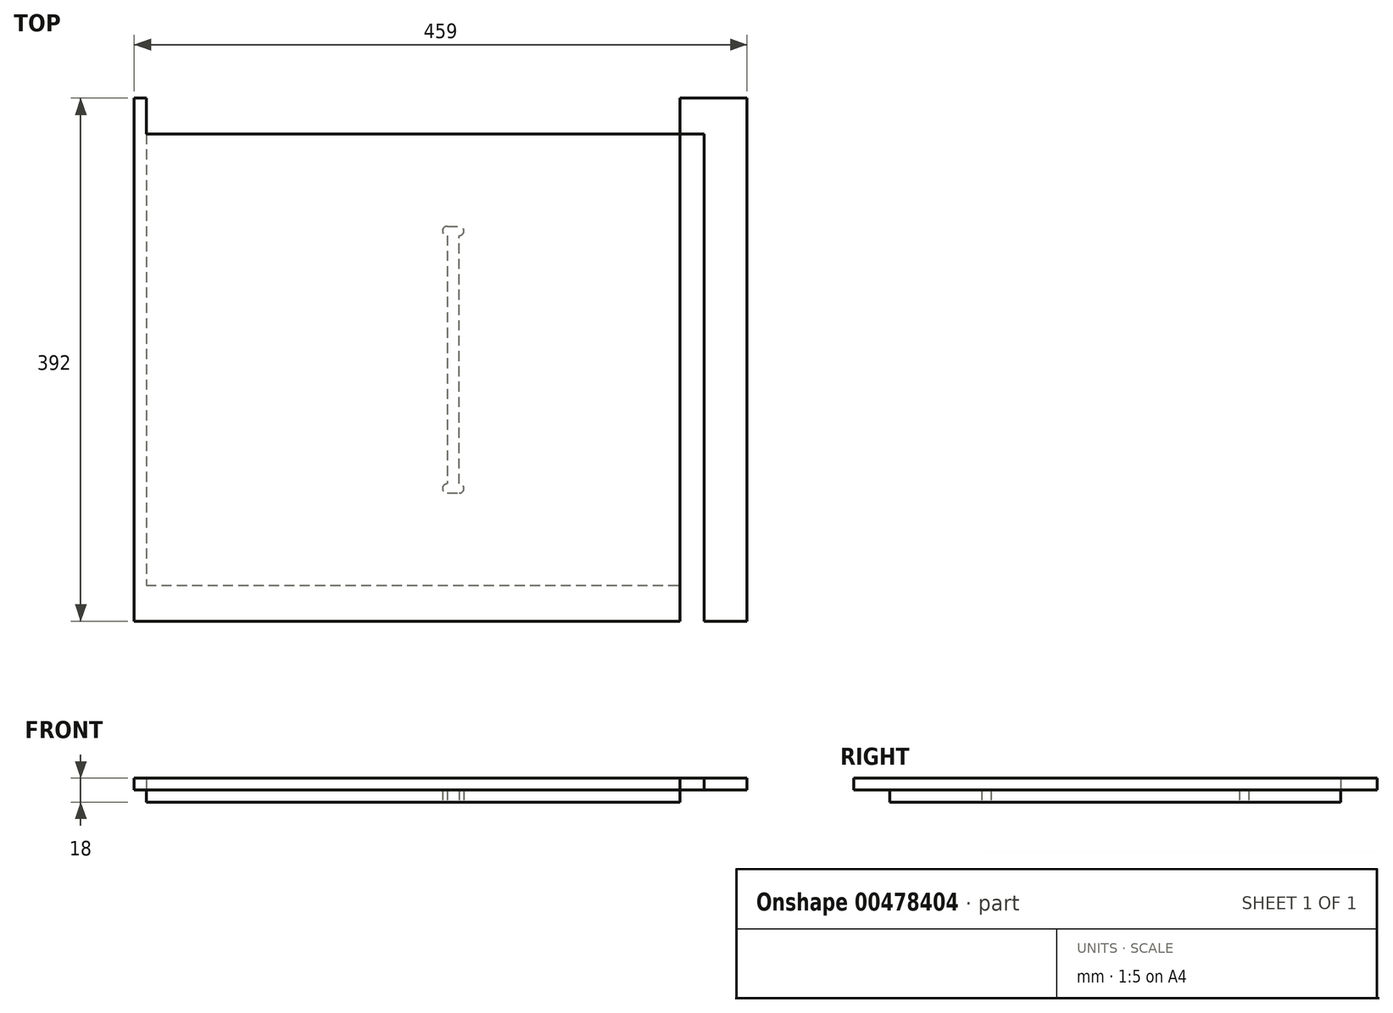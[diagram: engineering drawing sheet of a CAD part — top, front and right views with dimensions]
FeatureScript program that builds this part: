
annotation { "Feature Type Name" : "Feature", "Feature Type Description" : "" }
export const myFeature = defineFeature(function(context is Context, id is Id, definition is map)
    precondition{}
    {
        {
            var Q0;
            Q0=qCreatedBy(makeId("Top.planeOp"),FACE);
            var sketch = newSketch(context, id + "F0", { "sketchPlane" : qUnion([Q0])});
            skLineSegment(sketch, "E0.bottom", {"start": v(-966.15, 22.1) * mm, "end": v(-736.65, 22.1) * mm});
            skPoint(sketch, "E1", {"position": v(-736.65, 22.1) * mm});
            skPoint(sketch, "E2", {"position": v(-966.15, 22.1) * mm});
            skLineSegment(sketch, "E3.0", {"start": v(-966.15, -4.9) * mm, "end": v(133.85, -4.9) * mm});
            skLineSegment(sketch, "E4.0", {"start": v(-966.15, -369.9) * mm, "end": v(-736.65, -369.9) * mm});
            skLineSegment(sketch, "E5", {"start": v(-736.65, 22.1) * mm, "end": v(-736.65, -369.9) * mm, "construction": true});
            skLineSegment(sketch, "E6", {"start": v(-966.15, 22.1) * mm, "end": v(-966.15, -369.9) * mm});
            skLineSegment(sketch, "E7.0", {"start": v(-957.15, 22.1) * mm, "end": v(-957.15, -369.9) * mm});
            skLineSegment(sketch, "E8.0", {"start": v(-966.15, -342.9) * mm, "end": v(133.85, -342.9) * mm});
            skLineSegment(sketch, "E9.MirrorCS", {"start": v(-507.15, 22.1) * mm, "end": v(-507.15, -369.9) * mm});
            skPoint(sketch, "E10.MirrorP", {"position": v(-507.15, 22.1) * mm});
            skLineSegment(sketch, "E11.MirrorCS", {"start": v(-507.15, 22.1) * mm, "end": v(-736.65, 22.1) * mm});
            skLineSegment(sketch, "E12.MirrorCS", {"start": v(-507.15, -4.9) * mm, "end": v(-1607.15, -4.9) * mm});
            skLineSegment(sketch, "E13.MirrorCS", {"start": v(-507.15, -342.9) * mm, "end": v(-1607.15, -342.9) * mm});
            skLineSegment(sketch, "E14.MirrorCS", {"start": v(-507.15, -369.9) * mm, "end": v(-736.65, -369.9) * mm});
            skLineSegment(sketch, "E15", {"start": v(-731.6, -73.9) * mm, "end": v(-722.6, -73.9) * mm});
            skArc(sketch, "E16", {"start": v(-731.6, -73.9) * mm, "mid": v(-735.1, -77.4) * mm, "end": v(-731.6, -80.9) * mm});
            skArc(sketch, "E17", {"start": v(-722.6, -80.9) * mm, "mid": v(-719.1, -77.4) * mm, "end": v(-722.6, -73.9) * mm});
            skLineSegment(sketch, "E18.trimOffspring", {"start": v(-722.6, -80.9) * mm, "end": v(-722.6, -173.9) * mm});
            skLineSegment(sketch, "E19", {"start": v(-731.6, -80.9) * mm, "end": v(-731.6, -173.9) * mm});
            skLineSegment(sketch, "E20.MirrorCS", {"start": v(-722.6, -266.9) * mm, "end": v(-722.6, -173.9) * mm});
            skLineSegment(sketch, "E21.MirrorCS", {"start": v(-731.6, -266.9) * mm, "end": v(-731.6, -173.9) * mm});
            skArc(sketch, "E22.MirrorCS", {"start": v(-731.6, -273.9) * mm, "mid": v(-735.1, -270.4) * mm, "end": v(-731.6, -266.9) * mm});
            skLineSegment(sketch, "E23.MirrorCS", {"start": v(-731.6, -273.9) * mm, "end": v(-722.6, -273.9) * mm});
            skArc(sketch, "E24.MirrorCS", {"start": v(-722.6, -266.9) * mm, "mid": v(-719.1, -270.4) * mm, "end": v(-722.6, -273.9) * mm});
            skLineSegment(sketch, "E25.0", {"start": v(-539.15, 22.1) * mm, "end": v(-539.15, -369.9) * mm});
            skLineSegment(sketch, "E26.0", {"start": v(-557.15, 22.1) * mm, "end": v(-557.15, -369.9) * mm});
            skSolve(sketch);
        }
        {
            var Q0;
            {var subQ0=sQuery(id+"F0.wireOp",EDGE,"E6");var subQ1=sQuery(id+"F0.wireOp",EDGE,"E0.bottom");var subQ2=makeQuery(id+"F0.imprint","INTERSECT",VERTEX,{"derivedFrom":[subQ1,subQ0]});Q0=makeQuery(id+"F0.imprint","IMPRINT",FACE,{"disambiguationData":[TD([[makeQuery(id+"F0.imprint","IMPRINT",EDGE,{"disambiguationData":[TD([[subQ2,-1.0]])],"derivedFrom":subQ1}),-1.0]])]});}
            var Q1;
            {var subQ0=sQuery(id+"F0.wireOp",EDGE,"E6");var subQ1=sQuery(id+"F0.wireOp",EDGE,"E4.0");var subQ2=makeQuery(id+"F0.imprint","INTERSECT",VERTEX,{"derivedFrom":[subQ1,subQ0]});Q1=makeQuery(id+"F0.imprint","IMPRINT",FACE,{"disambiguationData":[TD([[makeQuery(id+"F0.imprint","IMPRINT",EDGE,{"disambiguationData":[TD([[subQ2,-1.0]])],"derivedFrom":subQ1}),1.0]])]});}
            var Q2;
            {var subQ0=sQuery(id+"F0.wireOp",EDGE,"E14.MirrorCS");var subQ1=sQuery(id+"F0.wireOp",EDGE,"E4.0");var subQ2=makeQuery(id+"F0.imprint","INTERSECT",VERTEX,{"derivedFrom":[subQ1,subQ0]});Q2=makeQuery(id+"F0.imprint","IMPRINT",FACE,{"disambiguationData":[TD([[makeQuery(id+"F0.imprint","IMPRINT",EDGE,{"disambiguationData":[TD([[subQ2,1.0]])],"derivedFrom":subQ1}),1.0]])]});}
            var Q3;
            {var subQ0=sQuery(id+"F0.wireOp",EDGE,"E25.0");var subQ1=sQuery(id+"F0.wireOp",EDGE,"E12.MirrorCS");var subQ2=makeQuery(id+"F0.imprint","INTERSECT",VERTEX,{"derivedFrom":[subQ1,subQ0]});Q3=makeQuery(id+"F0.imprint","IMPRINT",FACE,{"disambiguationData":[TD([[makeQuery(id+"F0.imprint","IMPRINT",EDGE,{"disambiguationData":[TD([[subQ2,-1.0]])],"derivedFrom":subQ1}),1.0]])]});}
            var Q4;
            {var subQ5=sQuery(id+"F0.wireOp",EDGE,"E0.bottom");var subQ7=sQuery(id+"F0.wireOp",EDGE,"E11.MirrorCS");var subQ9=makeQuery(id+"F0.imprint","INTERSECT",VERTEX,{"derivedFrom":[subQ5,subQ7]});Q4=makeQuery(id+"F0.imprint","IMPRINT",FACE,{"disambiguationData":[TD([[makeQuery(id+"F0.imprint","IMPRINT",EDGE,{"disambiguationData":[TD([[subQ9,1.0]])],"derivedFrom":subQ5}),-1.0]])]});}
            var Q5;
            Q5=makeQuery(id+"F0.imprint","IMPRINT",FACE,{"disambiguationData":[TD([[makeQuery(id+"F0.imprint","IMPRINT",EDGE,{"derivedFrom":sQuery(id+"F0.wireOp",EDGE,"E15")}),1.0]])]});
            var Q6;
            {var subQ0=sQuery(id+"F0.wireOp",EDGE,"E12.MirrorCS");var subQ1=sQuery(id+"F0.wireOp",EDGE,"E9.MirrorCS");var subQ2=makeQuery(id+"F0.imprint","INTERSECT",VERTEX,{"derivedFrom":[subQ1,subQ0]});Q6=makeQuery(id+"F0.imprint","IMPRINT",FACE,{"disambiguationData":[TD([[makeQuery(id+"F0.imprint","IMPRINT",EDGE,{"disambiguationData":[TD([[subQ2,1.0]])],"derivedFrom":subQ1}),-1.0]])]});}
            var Q7;
            {var subQ0=sQuery(id+"F0.wireOp",EDGE,"E12.MirrorCS");var subQ1=sQuery(id+"F0.wireOp",EDGE,"E9.MirrorCS");var subQ2=makeQuery(id+"F0.imprint","INTERSECT",VERTEX,{"derivedFrom":[subQ1,subQ0]});Q7=makeQuery(id+"F0.imprint","IMPRINT",FACE,{"disambiguationData":[TD([[makeQuery(id+"F0.imprint","IMPRINT",EDGE,{"disambiguationData":[TD([[subQ2,-1.0]])],"derivedFrom":subQ1}),-1.0]])]});}
            var Q8;
            {var subQ0=sQuery(id+"F0.wireOp",EDGE,"E12.MirrorCS");var subQ1=sQuery(id+"F0.wireOp",EDGE,"E6");var subQ2=makeQuery(id+"F0.imprint","INTERSECT",VERTEX,{"derivedFrom":[subQ1,subQ0]});Q8=makeQuery(id+"F0.imprint","IMPRINT",FACE,{"disambiguationData":[TD([[makeQuery(id+"F0.imprint","IMPRINT",EDGE,{"disambiguationData":[TD([[subQ2,-1.0]])],"derivedFrom":subQ1}),1.0]])]});}
            var Q9;
            Q9=makeQuery(id+"F0.imprint","IMPRINT",FACE,{"disambiguationData":[TD([[makeQuery(id+"F0.imprint","IMPRINT",EDGE,{"derivedFrom":sQuery(id+"F0.wireOp",EDGE,"E15")}),-1.0]])]});
            var Q10;
            {var subQ0=sQuery(id+"F0.wireOp",EDGE,"E25.0");var subQ1=sQuery(id+"F0.wireOp",EDGE,"E13.MirrorCS");var subQ2=makeQuery(id+"F0.imprint","INTERSECT",VERTEX,{"derivedFrom":[subQ1,subQ0]});Q10=makeQuery(id+"F0.imprint","IMPRINT",FACE,{"disambiguationData":[TD([[makeQuery(id+"F0.imprint","IMPRINT",EDGE,{"disambiguationData":[TD([[subQ2,-1.0]])],"derivedFrom":subQ1}),1.0]])]});}
            var Q11;
            {var subQ0=sQuery(id+"F0.wireOp",EDGE,"E25.0");var subQ1=sQuery(id+"F0.wireOp",EDGE,"E11.MirrorCS");var subQ2=makeQuery(id+"F0.imprint","INTERSECT",VERTEX,{"derivedFrom":[subQ1,subQ0]});Q11=makeQuery(id+"F0.imprint","IMPRINT",FACE,{"disambiguationData":[TD([[makeQuery(id+"F0.imprint","IMPRINT",EDGE,{"disambiguationData":[TD([[subQ2,-1.0]])],"derivedFrom":subQ1}),1.0]])]});}
            var Q12;
            {var subQ0=sQuery(id+"F0.wireOp",EDGE,"E13.MirrorCS");var subQ1=sQuery(id+"F0.wireOp",EDGE,"E9.MirrorCS");var subQ2=makeQuery(id+"F0.imprint","INTERSECT",VERTEX,{"derivedFrom":[subQ1,subQ0]});Q12=makeQuery(id+"F0.imprint","IMPRINT",FACE,{"disambiguationData":[TD([[makeQuery(id+"F0.imprint","IMPRINT",EDGE,{"disambiguationData":[TD([[subQ2,-1.0]])],"derivedFrom":subQ1}),-1.0]])]});}
            extrude(context, id + "F1", {"entities" : qUnion([Q0, Q1, Q2, Q3, Q4, Q5, Q6, Q7, Q8, Q9, Q10, Q11, Q12]), "depth" : 18 * mm});
        }
        {
            var Q0;
            {var subQ0=sQuery(id+"F0.wireOp",EDGE,"E6");var subQ1=sQuery(id+"F0.wireOp",EDGE,"E4.0");var subQ2=makeQuery(id+"F0.imprint","INTERSECT",VERTEX,{"derivedFrom":[subQ1,subQ0]});Q0=makeQuery(id+"F0.imprint","IMPRINT",FACE,{"disambiguationData":[TD([[makeQuery(id+"F0.imprint","IMPRINT",EDGE,{"disambiguationData":[TD([[subQ2,-1.0]])],"derivedFrom":subQ1}),1.0]])]});}
            var Q1;
            {var subQ0=sQuery(id+"F0.wireOp",EDGE,"E12.MirrorCS");var subQ1=sQuery(id+"F0.wireOp",EDGE,"E6");var subQ2=makeQuery(id+"F0.imprint","INTERSECT",VERTEX,{"derivedFrom":[subQ1,subQ0]});Q1=makeQuery(id+"F0.imprint","IMPRINT",FACE,{"disambiguationData":[TD([[makeQuery(id+"F0.imprint","IMPRINT",EDGE,{"disambiguationData":[TD([[subQ2,-1.0]])],"derivedFrom":subQ1}),1.0]])]});}
            var Q2;
            {var subQ0=sQuery(id+"F0.wireOp",EDGE,"E6");var subQ1=sQuery(id+"F0.wireOp",EDGE,"E0.bottom");var subQ2=makeQuery(id+"F0.imprint","INTERSECT",VERTEX,{"derivedFrom":[subQ1,subQ0]});Q2=makeQuery(id+"F0.imprint","IMPRINT",FACE,{"disambiguationData":[TD([[makeQuery(id+"F0.imprint","IMPRINT",EDGE,{"disambiguationData":[TD([[subQ2,-1.0]])],"derivedFrom":subQ1}),-1.0]])]});}
            var Q3;
            {var subQ5=sQuery(id+"F0.wireOp",EDGE,"E0.bottom");var subQ7=sQuery(id+"F0.wireOp",EDGE,"E11.MirrorCS");var subQ9=makeQuery(id+"F0.imprint","INTERSECT",VERTEX,{"derivedFrom":[subQ5,subQ7]});Q3=makeQuery(id+"F0.imprint","IMPRINT",FACE,{"disambiguationData":[TD([[makeQuery(id+"F0.imprint","IMPRINT",EDGE,{"disambiguationData":[TD([[subQ9,1.0]])],"derivedFrom":subQ5}),-1.0]])]});}
            var Q4;
            {var subQ0=sQuery(id+"F0.wireOp",EDGE,"E25.0");var subQ1=sQuery(id+"F0.wireOp",EDGE,"E11.MirrorCS");var subQ2=makeQuery(id+"F0.imprint","INTERSECT",VERTEX,{"derivedFrom":[subQ1,subQ0]});Q4=makeQuery(id+"F0.imprint","IMPRINT",FACE,{"disambiguationData":[TD([[makeQuery(id+"F0.imprint","IMPRINT",EDGE,{"disambiguationData":[TD([[subQ2,-1.0]])],"derivedFrom":subQ1}),1.0]])]});}
            var Q5;
            {var subQ0=sQuery(id+"F0.wireOp",EDGE,"E25.0");var subQ1=sQuery(id+"F0.wireOp",EDGE,"E12.MirrorCS");var subQ2=makeQuery(id+"F0.imprint","INTERSECT",VERTEX,{"derivedFrom":[subQ1,subQ0]});Q5=makeQuery(id+"F0.imprint","IMPRINT",FACE,{"disambiguationData":[TD([[makeQuery(id+"F0.imprint","IMPRINT",EDGE,{"disambiguationData":[TD([[subQ2,-1.0]])],"derivedFrom":subQ1}),1.0]])]});}
            var Q6;
            {var subQ0=sQuery(id+"F0.wireOp",EDGE,"E25.0");var subQ1=sQuery(id+"F0.wireOp",EDGE,"E13.MirrorCS");var subQ2=makeQuery(id+"F0.imprint","INTERSECT",VERTEX,{"derivedFrom":[subQ1,subQ0]});Q6=makeQuery(id+"F0.imprint","IMPRINT",FACE,{"disambiguationData":[TD([[makeQuery(id+"F0.imprint","IMPRINT",EDGE,{"disambiguationData":[TD([[subQ2,-1.0]])],"derivedFrom":subQ1}),1.0]])]});}
            var Q7;
            {var subQ0=sQuery(id+"F0.wireOp",EDGE,"E14.MirrorCS");var subQ1=sQuery(id+"F0.wireOp",EDGE,"E4.0");var subQ2=makeQuery(id+"F0.imprint","INTERSECT",VERTEX,{"derivedFrom":[subQ1,subQ0]});Q7=makeQuery(id+"F0.imprint","IMPRINT",FACE,{"disambiguationData":[TD([[makeQuery(id+"F0.imprint","IMPRINT",EDGE,{"disambiguationData":[TD([[subQ2,1.0]])],"derivedFrom":subQ1}),1.0]])]});}
            var Q8;
            Q8=makeQuery(id+"F0.imprint","IMPRINT",FACE,{"disambiguationData":[TD([[makeQuery(id+"F0.imprint","IMPRINT",EDGE,{"derivedFrom":sQuery(id+"F0.wireOp",EDGE,"E15")}),-1.0]])]});
            var Q9;
            {var subQ0=sQuery(id+"F0.wireOp",EDGE,"E12.MirrorCS");var subQ1=sQuery(id+"F0.wireOp",EDGE,"E9.MirrorCS");var subQ2=makeQuery(id+"F0.imprint","INTERSECT",VERTEX,{"derivedFrom":[subQ1,subQ0]});Q9=makeQuery(id+"F0.imprint","IMPRINT",FACE,{"disambiguationData":[TD([[makeQuery(id+"F0.imprint","IMPRINT",EDGE,{"disambiguationData":[TD([[subQ2,1.0]])],"derivedFrom":subQ1}),-1.0]])]});}
            var Q10;
            {var subQ0=sQuery(id+"F0.wireOp",EDGE,"E13.MirrorCS");var subQ1=sQuery(id+"F0.wireOp",EDGE,"E9.MirrorCS");var subQ2=makeQuery(id+"F0.imprint","INTERSECT",VERTEX,{"derivedFrom":[subQ1,subQ0]});Q10=makeQuery(id+"F0.imprint","IMPRINT",FACE,{"disambiguationData":[TD([[makeQuery(id+"F0.imprint","IMPRINT",EDGE,{"disambiguationData":[TD([[subQ2,-1.0]])],"derivedFrom":subQ1}),-1.0]])]});}
            extrude(context, id + "F2", {"entities" : qUnion([Q0, Q1, Q2, Q3, Q4, Q5, Q6, Q7, Q8, Q9, Q10]), "operationType" : NewBodyOperationType.REMOVE, "oppositeDirection" : true, "depth" : -9 * mm});
        }
    });
